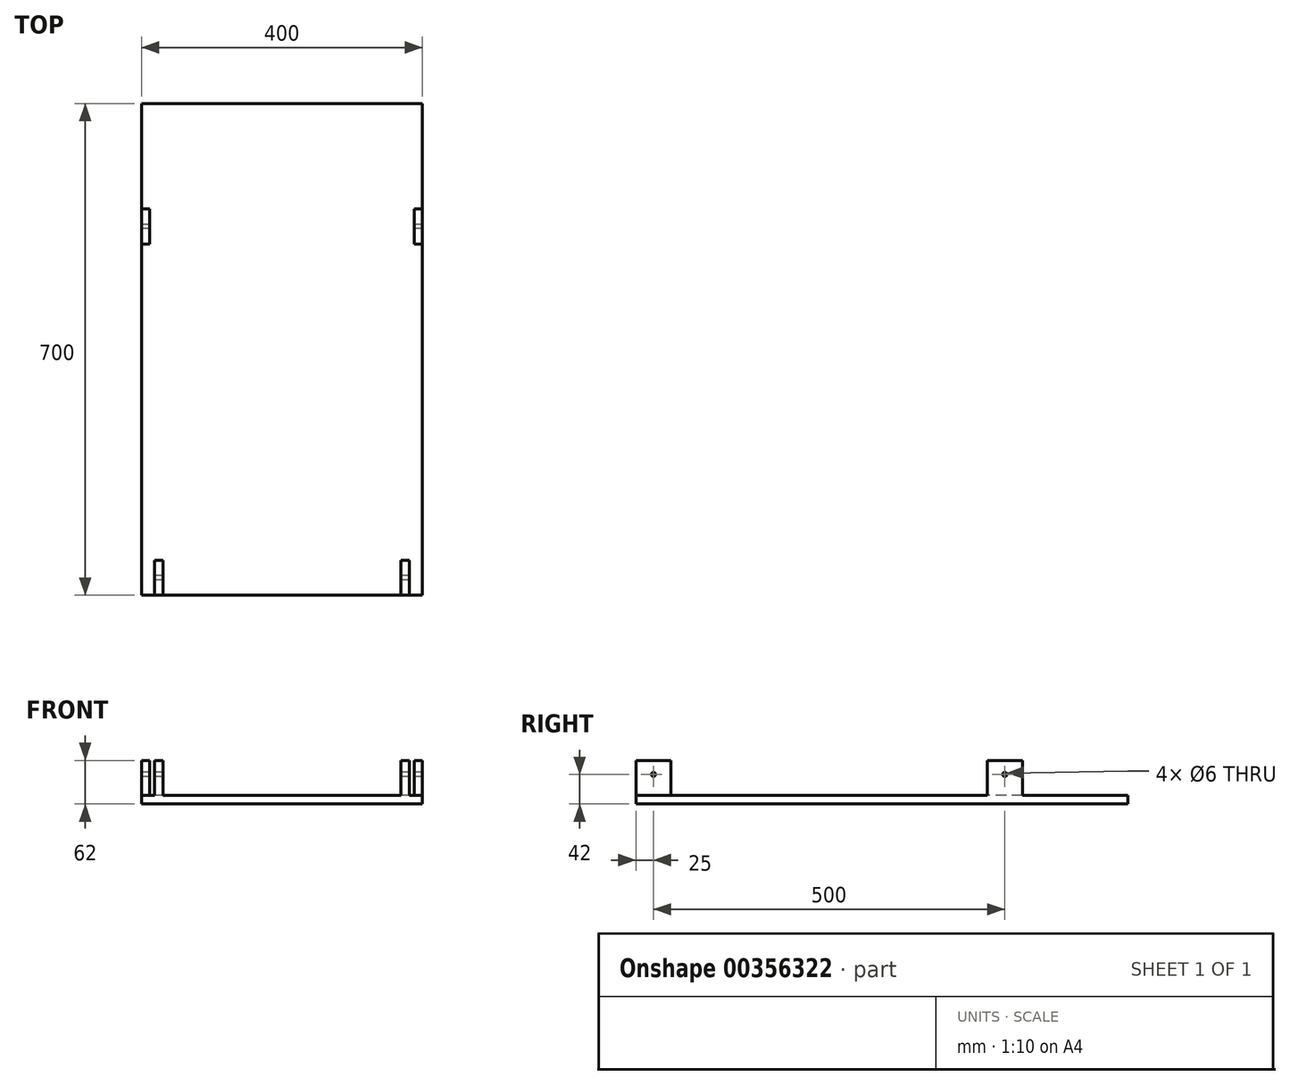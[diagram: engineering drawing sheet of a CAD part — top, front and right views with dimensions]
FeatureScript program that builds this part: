
annotation { "Feature Type Name" : "Feature", "Feature Type Description" : "" }
export const myFeature = defineFeature(function(context is Context, id is Id, definition is map)
    precondition{}
    {
        {
            var Q0;
            Q0=qCreatedBy(makeId("Front.planeOp"),FACE);
            var sketch = newSketch(context, id + "F0", { "sketchPlane" : qUnion([Q0])});
            skLineSegment(sketch, "E0.bottom", {"start": v(0, 0) * mm, "end": v(400, 0) * mm});
            skLineSegment(sketch, "E0.top", {"start": v(0, 12) * mm, "end": v(400, 12) * mm});
            skLineSegment(sketch, "E0.left", {"start": v(0, 0) * mm, "end": v(0, 12) * mm});
            skLineSegment(sketch, "E0.right", {"start": v(400, 0) * mm, "end": v(400, 12) * mm});
            skSolve(sketch);
        }
        {
            var Q0;
            Q0=makeQuery(id+"F0.imprint","IMPRINT",FACE,{"disambiguationData":[TD([[makeQuery(id+"F0.imprint","IMPRINT",EDGE,{"derivedFrom":sQuery(id+"F0.wireOp",EDGE,"E0.bottom")}),1.0]])]});
            extrude(context, id + "F1", {"entities" : qUnion([Q0]), "oppositeDirection" : true, "depth" : 700 * mm});
        }
        {
            var Q0;
            Q0=makeQuery(id+"F1.opExtrude","SWEPT_FACE",FACE,{"disambiguationData":[OSD([sQuery(id+"F0.wireOp",EDGE,"E0.top")])]});
            var sketch = newSketch(context, id + "F2", { "sketchPlane" : qUnion([Q0])});
            skLineSegment(sketch, "E1.bottom", {"start": v(31, 0) * mm, "end": v(19, 0) * mm});
            skLineSegment(sketch, "E1.top", {"start": v(31, 50) * mm, "end": v(19, 50) * mm});
            skLineSegment(sketch, "E1.left", {"start": v(31, 0) * mm, "end": v(31, 50) * mm});
            skLineSegment(sketch, "E1.right", {"start": v(19, 0) * mm, "end": v(19, 50) * mm});
            skLineSegment(sketch, "E2.bottom", {"start": v(381, 0) * mm, "end": v(369, 0) * mm});
            skLineSegment(sketch, "E2.top", {"start": v(381, 50) * mm, "end": v(369, 50) * mm});
            skLineSegment(sketch, "E2.left", {"start": v(381, 0) * mm, "end": v(381, 50) * mm});
            skLineSegment(sketch, "E2.right", {"start": v(369, 0) * mm, "end": v(369, 50) * mm});
            skLineSegment(sketch, "E3.bottom", {"start": v(0, 550) * mm, "end": v(12, 550) * mm});
            skLineSegment(sketch, "E3.top", {"start": v(0, 500) * mm, "end": v(12, 500) * mm});
            skLineSegment(sketch, "E3.left", {"start": v(0, 550) * mm, "end": v(0, 500) * mm});
            skLineSegment(sketch, "E3.right", {"start": v(12, 550) * mm, "end": v(12, 500) * mm});
            skLineSegment(sketch, "E4.bottom", {"start": v(388, 550) * mm, "end": v(400, 550) * mm});
            skLineSegment(sketch, "E4.top", {"start": v(388, 500) * mm, "end": v(400, 500) * mm});
            skLineSegment(sketch, "E4.left", {"start": v(388, 550) * mm, "end": v(388, 500) * mm});
            skLineSegment(sketch, "E4.right", {"start": v(400, 550) * mm, "end": v(400, 500) * mm});
            skSolve(sketch);
        }
        {
            var Q0;
            Q0=qSketchRegion(id+"F2",true);
            extrude(context, id + "F3", {"entities" : qUnion([Q0]), "operationType" : NewBodyOperationType.ADD, "depth" : 50 * mm});
        }
        {
            var Q0;
            Q0=makeQuery(id+"F3.opExtrude","SWEPT_FACE",FACE,{"disambiguationData":[OSD([sQuery(id+"F2.wireOp",EDGE,"E1.right")])]});
            var sketch = newSketch(context, id + "F4", { "sketchPlane" : qUnion([Q0])});
            skCircle(sketch, "E5", {"center": v(-25, 42) * mm, "radius": 3 * mm});
            skCircle(sketch, "E6", {"center": v(-525, 42) * mm, "radius": 3 * mm});
            skSolve(sketch);
        }
        {
            var Q0;
            Q0=qSketchRegion(id+"F4",true);
            extrude(context, id + "F5", {"entities" : qUnion([Q0]), "operationType" : NewBodyOperationType.REMOVE, "endBound" : BoundingType.THROUGH_ALL, "oppositeDirection" : true, "depth" : 25 * mm, "hasSecondDirection" : true, "secondDirectionBound" : SecondDirectionBoundingType.THROUGH_ALL, "secondDirectionOppositeDirection" : false, "secondDirectionDepth" : 25 * mm});
        }
    });
